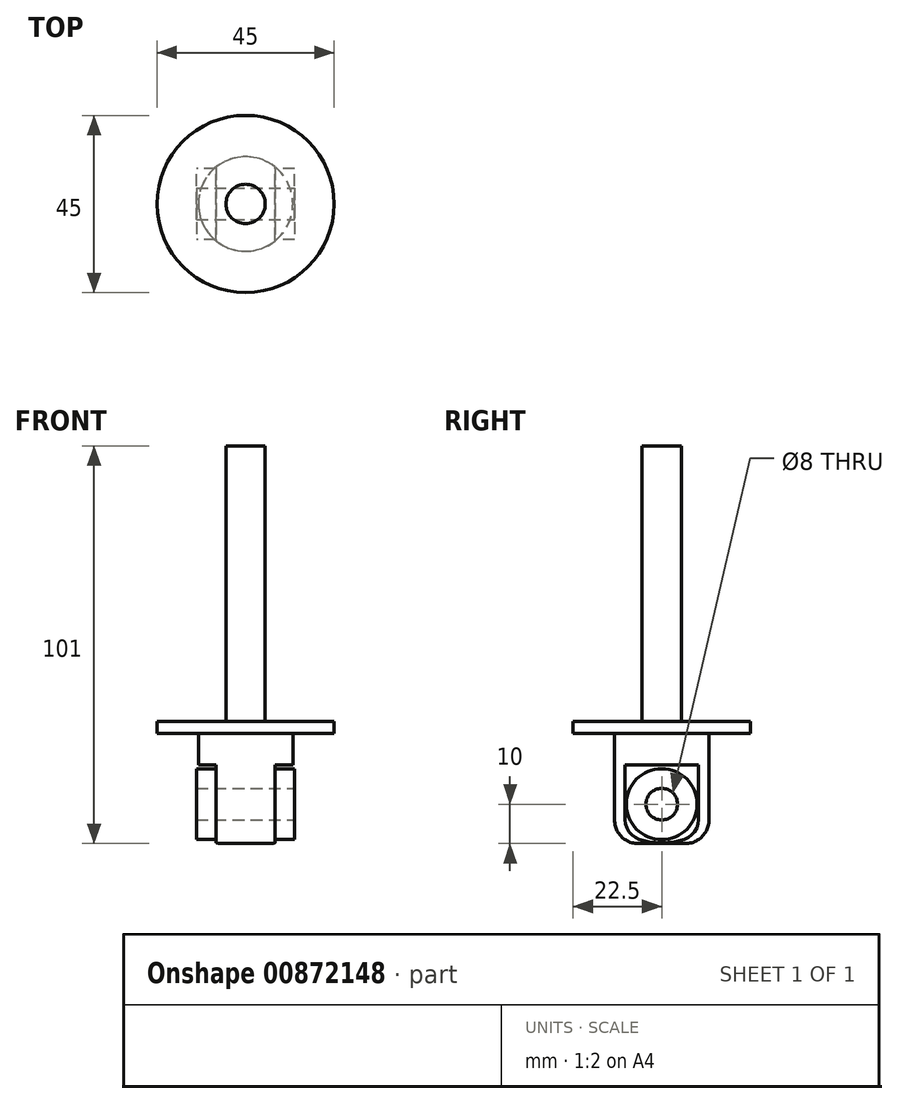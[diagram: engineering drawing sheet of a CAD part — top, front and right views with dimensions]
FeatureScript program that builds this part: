
annotation { "Feature Type Name" : "Feature", "Feature Type Description" : "" }
export const myFeature = defineFeature(function(context is Context, id is Id, definition is map)
    precondition{}
    {
        {
            var Q0;
            Q0=qCreatedBy(makeId("Top.planeOp"),FACE);
            var sketch = newSketch(context, id + "F0", { "sketchPlane" : qUnion([Q0])});
            skCircle(sketch, "E0", {"center": v(0, 0) * mm, "radius": 22.5 * mm});
            skSolve(sketch);
        }
        {
            var Q0;
            Q0 = qSketchRegion(id + "F0", true);
            extrude(context, id + "F1", {"entities" : qUnion([Q0]), "depth" : 3 * mm, "offsetDistance" : 25 * mm});
        }
        {
            var Q0;
            Q0=makeQuery(id+"F1.opExtrude","CAP_FACE",FACE,{"disambiguationData":[OSD([sQuery(id+"F0.wireOp",EDGE,"E0")])],"isStart":false});
            var sketch = newSketch(context, id + "F2", { "sketchPlane" : qUnion([Q0])});
            skCircle(sketch, "E1", {"center": v(0, 0) * mm, "radius": 5 * mm});
            skSolve(sketch);
        }
        {
            var Q0;
            Q0 = qSketchRegion(id + "F2", true);
            extrude(context, id + "F3", {"entities" : qUnion([Q0]), "operationType" : NewBodyOperationType.ADD, "depth" : 70 * mm, "offsetDistance" : 25 * mm});
        }
        {
            var Q0;
            Q0=makeQuery(id+"F1.opExtrude","CAP_FACE",FACE,{"disambiguationData":[OSD([sQuery(id+"F0.wireOp",EDGE,"E0")])],"isStart":true});
            var sketch = newSketch(context, id + "F4", { "sketchPlane" : qUnion([Q0])});
            skCircle(sketch, "E2", {"center": v(0, 0) * mm, "radius": 12 * mm});
            skSolve(sketch);
        }
        {
            var Q0;
            Q0 = qSketchRegion(id + "F4", true);
            extrude(context, id + "F5", {"entities" : qUnion([Q0]), "operationType" : NewBodyOperationType.ADD, "depth" : 28 * mm, "offsetDistance" : 25 * mm});
        }
        {
            var Q0;
            Q0=makeQuery(id+"F5.opExtrude","CAP_EDGE",EDGE,{"disambiguationData":[OSD([sQuery(id+"F4.wireOp",EDGE,"E2")])],"isStart":false});
            fillet(context, id + "F6", {"entities" : qUnion([Q0]), "radius" : 6 * mm, "tangentPropagation" : true, "allowEdgeOverflow" : false});
        }
        {
            var Q0;
            Q0=qCreatedBy(makeId("Front.planeOp"),FACE);
            var sketch = newSketch(context, id + "F7", { "sketchPlane" : qUnion([Q0])});
            skLineSegment(sketch, "E3", {"start": v(0, 0) * mm, "end": v(0, -45.1) * mm, "construction": true});
            skLineSegment(sketch, "E4", {"start": v(7.5, -28) * mm, "end": v(27.07, -28) * mm});
            skLineSegment(sketch, "E5", {"start": v(27.07, -28) * mm, "end": v(27.07, -8) * mm});
            skLineSegment(sketch, "E6", {"start": v(27.07, -8) * mm, "end": v(7.5, -8) * mm});
            skLineSegment(sketch, "E7", {"start": v(7.5, -8) * mm, "end": v(7.5, -28) * mm});
            skLineSegment(sketch, "E8.MirrorCS", {"start": v(-27.07, -8) * mm, "end": v(-7.5, -8) * mm});
            skLineSegment(sketch, "E9.MirrorCS", {"start": v(-7.5, -8) * mm, "end": v(-7.5, -28) * mm});
            skLineSegment(sketch, "E10.MirrorCS", {"start": v(-27.07, -28) * mm, "end": v(-27.07, -8) * mm});
            skLineSegment(sketch, "E11.MirrorCS", {"start": v(-7.5, -28) * mm, "end": v(-27.07, -28) * mm});
            skSolve(sketch);
        }
        {
            var Q0;
            Q0=makeQuery(id+"F7.imprint","IMPRINT",FACE,{"disambiguationData":[TD([[makeQuery(id+"F7.imprint","IMPRINT",EDGE,{"derivedFrom":sQuery(id+"F7.wireOp",EDGE,"E4")}),1.0]])]});
            var Q1;
            Q1=makeQuery(id+"F7.imprint","IMPRINT",FACE,{"disambiguationData":[TD([[makeQuery(id+"F7.imprint","IMPRINT",EDGE,{"derivedFrom":sQuery(id+"F7.wireOp",EDGE,"E8.MirrorCS")}),-1.0]])]});
            extrude(context, id + "F8", {"entities" : qUnion([Q0, Q1]), "operationType" : NewBodyOperationType.REMOVE, "endBound" : BoundingType.SYMMETRIC, "oppositeDirection" : true, "depth" : 100 * mm, "offsetDistance" : 25 * mm});
        }
        {
            var Q0;
            Q0=makeQuery(id+"F8.boolean.opBoolean","COPY",FACE,{"derivedFrom":makeQuery(id+"F8.opExtrude","SWEPT_FACE",FACE,{"disambiguationData":[OSD([sQuery(id+"F7.wireOp",EDGE,"E7")])]})});
            var sketch = newSketch(context, id + "F9", { "sketchPlane" : qUnion([Q0])});
            skLineSegment(sketch, "E12", {"start": v(0, 0) * mm, "end": v(0, -50.87) * mm, "construction": true});
            skPoint(sketch, "E12.endSnap0", {"position": v(0, -8) * mm});
            skCircle(sketch, "E13", {"center": v(0, -18) * mm, "radius": 4 * mm});
            skSolve(sketch);
        }
        {
            var Q0;
            Q0 = qSketchRegion(id + "F9", true);
            extrude(context, id + "F10", {"entities" : qUnion([Q0]), "operationType" : NewBodyOperationType.REMOVE, "endBound" : BoundingType.THROUGH_ALL, "oppositeDirection" : true, "depth" : 25 * mm, "offsetDistance" : 25 * mm});
        }
        {
            var Q0;
            Q0=qCreatedBy(makeId("Right.planeOp"),FACE);
            var sketch = newSketch(context, id + "F11", { "sketchPlane" : qUnion([Q0])});
            skCircle(sketch, "E14", {"center": v(0, -18) * mm, "radius": 9 * mm});
            skSolve(sketch);
        }
        {
            var Q0;
            Q0=makeQuery(id+"F11.imprint","IMPRINT",FACE,{"disambiguationData":[TD([[makeQuery(id+"F11.imprint","IMPRINT",EDGE,{"derivedFrom":sQuery(id+"F11.wireOp",EDGE,"E14")}),1.0]])]});
            var sketch = newSketch(context, id + "F12", { "sketchPlane" : qUnion([Q0])});
            skCircle(sketch, "E15.0", {"center": v(0, -18) * mm, "radius": 9 * mm});
            skSolve(sketch);
        }
        {
            var Q0;
            Q0 = qSketchRegion(id + "F12", true);
            extrude(context, id + "F13", {"entities" : qUnion([Q0]), "operationType" : NewBodyOperationType.ADD, "endBound" : BoundingType.SYMMETRIC, "depth" : 25 * mm, "offsetDistance" : 25 * mm});
        }
        {
            var Q0;
            Q0=makeQuery(id+"F13.opExtrude","CAP_FACE",FACE,{"disambiguationData":[OSD([sQuery(id+"F12.wireOp",EDGE,"E15.0")])],"isStart":false});
            var sketch = newSketch(context, id + "F14", { "sketchPlane" : qUnion([Q0])});
            skCircle(sketch, "E16", {"center": v(0, -18) * mm, "radius": 4 * mm});
            skSolve(sketch);
        }
        {
            var Q0;
            Q0 = qSketchRegion(id + "F14", true);
            extrude(context, id + "F15", {"entities" : qUnion([Q0]), "operationType" : NewBodyOperationType.REMOVE, "endBound" : BoundingType.SYMMETRIC, "oppositeDirection" : true, "depth" : 100 * mm, "offsetDistance" : 25 * mm});
        }
    });
